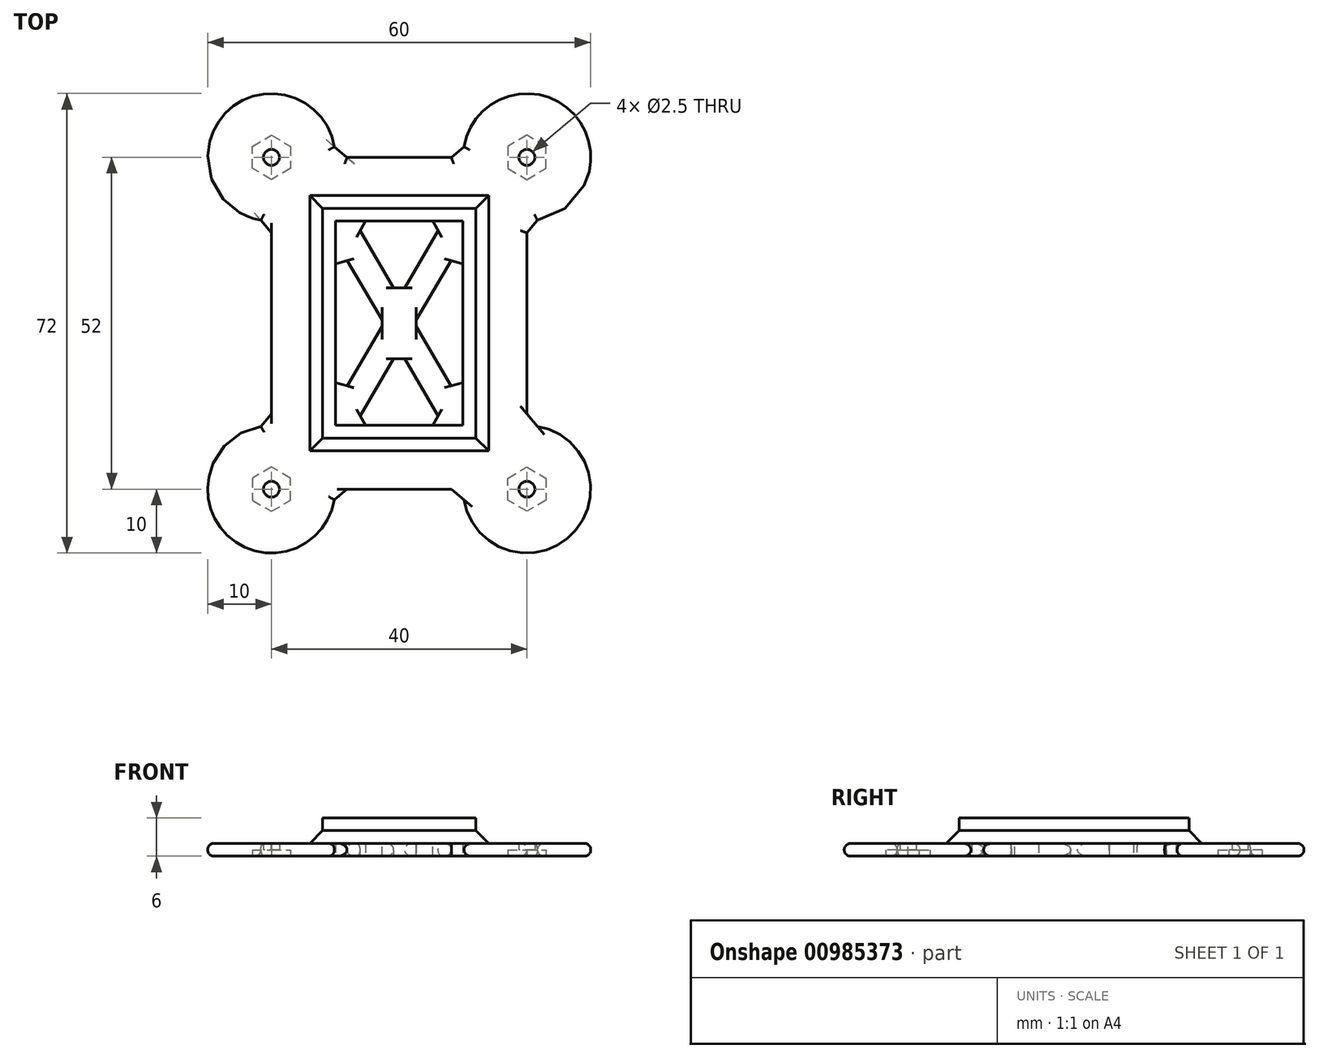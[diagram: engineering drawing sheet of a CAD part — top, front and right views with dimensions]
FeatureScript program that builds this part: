
annotation { "Feature Type Name" : "Feature", "Feature Type Description" : "" }
export const myFeature = defineFeature(function(context is Context, id is Id, definition is map)
    precondition{}
    {
        {
            var Q0;
            Q0=qCreatedBy(makeId("Top.planeOp"),FACE);
            var sketch = newSketch(context, id + "F0", { "sketchPlane" : qUnion([Q0])});
            skPoint(sketch, "E0.middle", {"position": v(0, 0) * mm});
            skLineSegment(sketch, "E1.bottom", {"start": v(10, -16) * mm, "end": v(-10, -16) * mm});
            skLineSegment(sketch, "E1.top", {"start": v(10, 16) * mm, "end": v(-10, 16) * mm});
            skLineSegment(sketch, "E1.left", {"start": v(10, -16) * mm, "end": v(10, 16) * mm});
            skLineSegment(sketch, "E1.right", {"start": v(-10, -16) * mm, "end": v(-10, 16) * mm});
            skLineSegment(sketch, "E2.bottom", {"start": v(12, 18) * mm, "end": v(-12, 18) * mm});
            skLineSegment(sketch, "E2.top", {"start": v(12, -18) * mm, "end": v(-12, -18) * mm});
            skLineSegment(sketch, "E2.left", {"start": v(12, 18) * mm, "end": v(12, -18) * mm});
            skLineSegment(sketch, "E2.right", {"start": v(-12, 18) * mm, "end": v(-12, -18) * mm});
            skLineSegment(sketch, "E3.bottom", {"start": v(20, -26) * mm, "end": v(-20, -26) * mm});
            skLineSegment(sketch, "E3.top", {"start": v(20, 26) * mm, "end": v(-20, 26) * mm});
            skLineSegment(sketch, "E3.left", {"start": v(20, -26) * mm, "end": v(20, 26) * mm});
            skLineSegment(sketch, "E3.right", {"start": v(-20, -26) * mm, "end": v(-20, 26) * mm});
            skCircle(sketch, "E4", {"center": v(-20, 26) * mm, "radius": 10 * mm});
            skCircle(sketch, "E5", {"center": v(20, 26) * mm, "radius": 10 * mm});
            skCircle(sketch, "E6", {"center": v(20, -26) * mm, "radius": 10 * mm});
            skCircle(sketch, "E7", {"center": v(-20, -26) * mm, "radius": 10 * mm});
            skCircle(sketch, "E8", {"center": v(-20, 26) * mm, "radius": 1.25 * mm});
            skCircle(sketch, "E9.MirrorC", {"center": v(20, 26) * mm, "radius": 1.25 * mm});
            skCircle(sketch, "E10.MirrorC", {"center": v(-20, -26) * mm, "radius": 1.25 * mm});
            skCircle(sketch, "E11.MirrorC", {"center": v(20, -26) * mm, "radius": 1.25 * mm});
            skCircle(sketch, "E12.cCircle", {"center": v(20, -26) * mm, "radius": 3 * mm, "construction": true});
            skLineSegment(sketch, "E12.0", {"start": v(23, -24.27) * mm, "end": v(23, -27.73) * mm});
            skLineSegment(sketch, "E12.1", {"start": v(23, -27.73) * mm, "end": v(20, -29.46) * mm});
            skLineSegment(sketch, "E12.2", {"start": v(20, -29.46) * mm, "end": v(17, -27.73) * mm});
            skLineSegment(sketch, "E12.3", {"start": v(17, -27.73) * mm, "end": v(17, -24.27) * mm});
            skLineSegment(sketch, "E12.4", {"start": v(17, -24.27) * mm, "end": v(20, -22.54) * mm});
            skLineSegment(sketch, "E12.5", {"start": v(20, -22.54) * mm, "end": v(23, -24.27) * mm});
            skPoint(sketch, "E12.0.midPoint", {"position": v(23, -26) * mm});
            skLineSegment(sketch, "E13.MirrorCS", {"start": v(-17, -27.73) * mm, "end": v(-17, -24.27) * mm});
            skLineSegment(sketch, "E14.MirrorCS", {"start": v(-20, -22.54) * mm, "end": v(-23, -24.27) * mm});
            skLineSegment(sketch, "E15.MirrorCS", {"start": v(-20, -29.46) * mm, "end": v(-17, -27.73) * mm});
            skLineSegment(sketch, "E16.MirrorCS", {"start": v(-23, -27.73) * mm, "end": v(-20, -29.46) * mm});
            skCircle(sketch, "E17.MirrorC", {"center": v(-20, -26) * mm, "radius": 3 * mm, "construction": true});
            skLineSegment(sketch, "E18.MirrorCS", {"start": v(-20, -26) * mm, "end": v(20, -26) * mm});
            skLineSegment(sketch, "E19.MirrorCS", {"start": v(-23, -24.27) * mm, "end": v(-23, -27.73) * mm});
            skLineSegment(sketch, "E20.MirrorCS", {"start": v(-17, -24.27) * mm, "end": v(-20, -22.54) * mm});
            skPoint(sketch, "E21.MirrorP", {"position": v(-23, -26) * mm});
            skCircle(sketch, "E22.MirrorC", {"center": v(20, 26) * mm, "radius": 3 * mm, "construction": true});
            skPoint(sketch, "E23.MirrorP", {"position": v(23, 26) * mm});
            skLineSegment(sketch, "E24.MirrorCS", {"start": v(20, 22.54) * mm, "end": v(23, 24.27) * mm});
            skLineSegment(sketch, "E25.MirrorCS", {"start": v(23, 27.73) * mm, "end": v(20, 29.46) * mm});
            skLineSegment(sketch, "E26.MirrorCS", {"start": v(23, 24.27) * mm, "end": v(23, 27.73) * mm});
            skLineSegment(sketch, "E27.MirrorCS", {"start": v(17, 27.73) * mm, "end": v(17, 24.27) * mm});
            skLineSegment(sketch, "E28.MirrorCS", {"start": v(17, 24.27) * mm, "end": v(20, 22.54) * mm});
            skLineSegment(sketch, "E29.MirrorCS", {"start": v(20, 29.46) * mm, "end": v(17, 27.73) * mm});
            skCircle(sketch, "E30.MirrorC", {"center": v(-20, 26) * mm, "radius": 3 * mm, "construction": true});
            skLineSegment(sketch, "E31.MirrorCS", {"start": v(-20, 26) * mm, "end": v(20, 26) * mm});
            skPoint(sketch, "E32.MirrorP", {"position": v(-23, 26) * mm});
            skLineSegment(sketch, "E33.MirrorCS", {"start": v(-20, 22.54) * mm, "end": v(-23, 24.27) * mm});
            skLineSegment(sketch, "E34.MirrorCS", {"start": v(-20, 26) * mm, "end": v(-20, -26) * mm});
            skLineSegment(sketch, "E35.MirrorCS", {"start": v(-23, 24.27) * mm, "end": v(-23, 27.73) * mm});
            skLineSegment(sketch, "E36.MirrorCS", {"start": v(-23, 27.73) * mm, "end": v(-20, 29.46) * mm});
            skLineSegment(sketch, "E37.MirrorCS", {"start": v(-17, 24.27) * mm, "end": v(-20, 22.54) * mm});
            skLineSegment(sketch, "E38.MirrorCS", {"start": v(-20, 29.46) * mm, "end": v(-17, 27.73) * mm});
            skLineSegment(sketch, "E39.MirrorCS", {"start": v(-17, 27.73) * mm, "end": v(-17, 24.27) * mm});
            skLineSegment(sketch, "E40", {"start": v(-10, 13) * mm, "end": v(7, -16) * mm});
            skLineSegment(sketch, "E41", {"start": v(-7, 16) * mm, "end": v(10, -13) * mm});
            skLineSegment(sketch, "E42", {"start": v(10, 13) * mm, "end": v(-7, -16) * mm});
            skLineSegment(sketch, "E43", {"start": v(7, 16) * mm, "end": v(-10, -13) * mm});
            skSolve(sketch);
        }
        {
            var Q0;
            Q0=makeQuery(id+"F0.imprint","IMPRINT",FACE,{"disambiguationData":[TD([[makeQuery(id+"F0.imprint","IMPRINT",EDGE,{"derivedFrom":sQuery(id+"F0.wireOp",EDGE,"E1.bottom")}),1.0]])]});
            var Q1;
            {var subQ0=sQuery(id+"F0.wireOp",EDGE,"XfmaCdGe-Nsh5-LR8N-U050-nXJdRo87k7nu");Q1=makeQuery(id+"F0.imprint","IMPRINT",FACE,{"disambiguationData":[TD([[makeQuery(id+"F0.imprint","IMPRINT",EDGE,{"derivedFrom":subQ0}),-1.0]])]});}
            var Q2;
            {var subQ0=sQuery(id+"F0.wireOp",EDGE,"67c493aa-9df7-43f4-b791-e47cdcb916b60.MirrorCS");Q2=makeQuery(id+"F0.imprint","IMPRINT",FACE,{"disambiguationData":[TD([[makeQuery(id+"F0.imprint","IMPRINT",EDGE,{"derivedFrom":subQ0}),-1.0]])]});}
            var Q3;
            {var subQ0=sQuery(id+"F0.wireOp",EDGE,"3c266ea2-0ddf-4ded-b89f-077357a7d8e80.MirrorCS");Q3=makeQuery(id+"F0.imprint","IMPRINT",FACE,{"disambiguationData":[TD([[makeQuery(id+"F0.imprint","IMPRINT",EDGE,{"derivedFrom":subQ0}),-1.0]])]});}
            var Q4;
            {var subQ0=sQuery(id+"F0.wireOp",EDGE,"ab4d64e5-a29a-4c87-9f54-f3676ced8fba0.MirrorCS");Q4=makeQuery(id+"F0.imprint","IMPRINT",FACE,{"disambiguationData":[TD([[makeQuery(id+"F0.imprint","IMPRINT",EDGE,{"derivedFrom":subQ0}),1.0]])]});}
            var Q5;
            Q5=makeQuery(id+"F0.imprint","IMPRINT",FACE,{"disambiguationData":[TD([[makeQuery(id+"F0.imprint","IMPRINT",EDGE,{"derivedFrom":sQuery(id+"F0.wireOp",EDGE,"oP3ZfhLO-5z78-oQSo-uuvH-yzJxo6IJEnQO")}),-1.0]])]});
            var Q6;
            Q6=makeQuery(id+"F0.imprint","IMPRINT",FACE,{"disambiguationData":[TD([[makeQuery(id+"F0.imprint","IMPRINT",EDGE,{"derivedFrom":sQuery(id+"F0.wireOp",EDGE,"5d5cfb4f-1e90-434a-910e-95713f9e32be0.MirrorC")}),1.0]])]});
            var Q7;
            Q7=makeQuery(id+"F0.imprint","IMPRINT",FACE,{"disambiguationData":[TD([[makeQuery(id+"F0.imprint","IMPRINT",EDGE,{"derivedFrom":sQuery(id+"F0.wireOp",EDGE,"24c43ebd-9ed0-4dd5-8c82-3635907a6bdc0.MirrorC")}),-1.0]])]});
            var Q8;
            Q8=makeQuery(id+"F0.imprint","IMPRINT",FACE,{"disambiguationData":[TD([[makeQuery(id+"F0.imprint","IMPRINT",EDGE,{"derivedFrom":sQuery(id+"F0.wireOp",EDGE,"ed7e95fd-fa47-4424-be7c-35b6ced3335c0.MirrorC")}),1.0]])]});
            var Q9;
            Q9=makeQuery(id+"F0.imprint","IMPRINT",FACE,{"disambiguationData":[TD([[makeQuery(id+"F0.imprint","IMPRINT",EDGE,{"derivedFrom":sQuery(id+"F0.wireOp",EDGE,"E2.bottom")}),-1.0]])]});
            var Q10;
            {var subQ0=sQuery(id+"F0.wireOp",EDGE,"E4");var subQ1=sQuery(id+"F0.wireOp",EDGE,"E3.top");var subQ2=makeQuery(id+"F0.imprint","INTERSECT",VERTEX,{"derivedFrom":[subQ1,subQ0]});Q10=makeQuery(id+"F0.imprint","IMPRINT",FACE,{"disambiguationData":[TD([[makeQuery(id+"F0.imprint","IMPRINT",EDGE,{"disambiguationData":[TD([[subQ2,-1.0]])],"derivedFrom":subQ1}),1.0]])]});}
            var Q11;
            {var subQ0=sQuery(id+"F0.wireOp",EDGE,"E4");var subQ1=sQuery(id+"F0.wireOp",EDGE,"E3.top");var subQ2=makeQuery(id+"F0.imprint","INTERSECT",VERTEX,{"derivedFrom":[subQ1,subQ0]});Q11=makeQuery(id+"F0.imprint","IMPRINT",FACE,{"disambiguationData":[TD([[makeQuery(id+"F0.imprint","IMPRINT",EDGE,{"disambiguationData":[TD([[subQ2,-1.0]])],"derivedFrom":subQ1}),-1.0]])]});}
            var Q12;
            {var subQ0=sQuery(id+"F0.wireOp",EDGE,"E5");var subQ1=sQuery(id+"F0.wireOp",EDGE,"E3.top");var subQ2=makeQuery(id+"F0.imprint","INTERSECT",VERTEX,{"derivedFrom":[subQ1,subQ0]});Q12=makeQuery(id+"F0.imprint","IMPRINT",FACE,{"disambiguationData":[TD([[makeQuery(id+"F0.imprint","IMPRINT",EDGE,{"disambiguationData":[TD([[subQ2,1.0]])],"derivedFrom":subQ1}),1.0]])]});}
            var Q13;
            {var subQ0=sQuery(id+"F0.wireOp",EDGE,"E5");var subQ1=sQuery(id+"F0.wireOp",EDGE,"E3.top");var subQ2=makeQuery(id+"F0.imprint","INTERSECT",VERTEX,{"derivedFrom":[subQ1,subQ0]});Q13=makeQuery(id+"F0.imprint","IMPRINT",FACE,{"disambiguationData":[TD([[makeQuery(id+"F0.imprint","IMPRINT",EDGE,{"disambiguationData":[TD([[subQ2,1.0]])],"derivedFrom":subQ1}),-1.0]])]});}
            var Q14;
            {var subQ0=sQuery(id+"F0.wireOp",EDGE,"E6");var subQ1=sQuery(id+"F0.wireOp",EDGE,"E3.bottom");var subQ2=makeQuery(id+"F0.imprint","INTERSECT",VERTEX,{"derivedFrom":[subQ1,subQ0]});Q14=makeQuery(id+"F0.imprint","IMPRINT",FACE,{"disambiguationData":[TD([[makeQuery(id+"F0.imprint","IMPRINT",EDGE,{"disambiguationData":[TD([[subQ2,1.0]])],"derivedFrom":subQ1}),-1.0]])]});}
            var Q15;
            {var subQ0=sQuery(id+"F0.wireOp",EDGE,"E6");var subQ1=sQuery(id+"F0.wireOp",EDGE,"E3.bottom");var subQ2=makeQuery(id+"F0.imprint","INTERSECT",VERTEX,{"derivedFrom":[subQ1,subQ0]});Q15=makeQuery(id+"F0.imprint","IMPRINT",FACE,{"disambiguationData":[TD([[makeQuery(id+"F0.imprint","IMPRINT",EDGE,{"disambiguationData":[TD([[subQ2,1.0]])],"derivedFrom":subQ1}),1.0]])]});}
            var Q16;
            {var subQ0=sQuery(id+"F0.wireOp",EDGE,"E7");var subQ1=sQuery(id+"F0.wireOp",EDGE,"E3.bottom");var subQ2=makeQuery(id+"F0.imprint","INTERSECT",VERTEX,{"derivedFrom":[subQ1,subQ0]});Q16=makeQuery(id+"F0.imprint","IMPRINT",FACE,{"disambiguationData":[TD([[makeQuery(id+"F0.imprint","IMPRINT",EDGE,{"disambiguationData":[TD([[subQ2,-1.0]])],"derivedFrom":subQ1}),1.0]])]});}
            var Q17;
            {var subQ0=sQuery(id+"F0.wireOp",EDGE,"E7");var subQ1=sQuery(id+"F0.wireOp",EDGE,"E3.bottom");var subQ2=makeQuery(id+"F0.imprint","INTERSECT",VERTEX,{"derivedFrom":[subQ1,subQ0]});Q17=makeQuery(id+"F0.imprint","IMPRINT",FACE,{"disambiguationData":[TD([[makeQuery(id+"F0.imprint","IMPRINT",EDGE,{"disambiguationData":[TD([[subQ2,-1.0]])],"derivedFrom":subQ1}),-1.0]])]});}
            var Q18;
            {var subQ0=sQuery(id+"F0.wireOp",EDGE,"E15.MirrorCS");Q18=makeQuery(id+"F0.imprint","IMPRINT",FACE,{"disambiguationData":[TD([[makeQuery(id+"F0.imprint","IMPRINT",EDGE,{"derivedFrom":subQ0}),-1.0]])]});}
            var Q19;
            {var subQ0=sQuery(id+"F0.wireOp",EDGE,"E12.4");Q19=makeQuery(id+"F0.imprint","IMPRINT",FACE,{"disambiguationData":[TD([[makeQuery(id+"F0.imprint","IMPRINT",EDGE,{"derivedFrom":subQ0}),1.0]])]});}
            var Q20;
            Q20=makeQuery(id+"F0.imprint","IMPRINT",FACE,{"disambiguationData":[TD([[makeQuery(id+"F0.imprint","IMPRINT",EDGE,{"derivedFrom":sQuery(id+"F0.wireOp",EDGE,"E12.0")}),1.0]])]});
            var Q21;
            {var subQ5=sQuery(id+"F0.wireOp",EDGE,"E20.MirrorCS");Q21=makeQuery(id+"F0.imprint","IMPRINT",FACE,{"disambiguationData":[TD([[makeQuery(id+"F0.imprint","IMPRINT",EDGE,{"derivedFrom":subQ5}),-1.0]])]});}
            var Q22;
            {var subQ0=sQuery(id+"F0.wireOp",EDGE,"E38.MirrorCS");Q22=makeQuery(id+"F0.imprint","IMPRINT",FACE,{"disambiguationData":[TD([[makeQuery(id+"F0.imprint","IMPRINT",EDGE,{"derivedFrom":subQ0}),1.0]])]});}
            var Q23;
            {var subQ0=sQuery(id+"F0.wireOp",EDGE,"E37.MirrorCS");Q23=makeQuery(id+"F0.imprint","IMPRINT",FACE,{"disambiguationData":[TD([[makeQuery(id+"F0.imprint","IMPRINT",EDGE,{"derivedFrom":subQ0}),1.0]])]});}
            var Q24;
            {var subQ0=sQuery(id+"F0.wireOp",EDGE,"E28.MirrorCS");Q24=makeQuery(id+"F0.imprint","IMPRINT",FACE,{"disambiguationData":[TD([[makeQuery(id+"F0.imprint","IMPRINT",EDGE,{"derivedFrom":subQ0}),-1.0]])]});}
            var Q25;
            {var subQ5=sQuery(id+"F0.wireOp",EDGE,"E24.MirrorCS");Q25=makeQuery(id+"F0.imprint","IMPRINT",FACE,{"disambiguationData":[TD([[makeQuery(id+"F0.imprint","IMPRINT",EDGE,{"derivedFrom":subQ5}),-1.0]])]});}
            var Q26;
            {var subQ1=sQuery(id+"F0.wireOp",EDGE,"E1.left");var subQ5=sQuery(id+"F0.wireOp",EDGE,"E1.bottom");var subQ6=makeQuery(id+"F0.imprint","INTERSECT",VERTEX,{"derivedFrom":[subQ5,subQ1]});Q26=makeQuery(id+"F0.imprint","IMPRINT",FACE,{"disambiguationData":[TD([[makeQuery(id+"F0.imprint","IMPRINT",EDGE,{"disambiguationData":[TD([[subQ6,-1.0]])],"derivedFrom":subQ5}),-1.0]])]});}
            var Q27;
            {var subQ0=sQuery(id+"F0.wireOp",EDGE,"E43");var subQ1=sQuery(id+"F0.wireOp",EDGE,"E40");var subQ2=makeQuery(id+"F0.imprint","INTERSECT",VERTEX,{"derivedFrom":[subQ1,subQ0]});Q27=makeQuery(id+"F0.imprint","IMPRINT",FACE,{"disambiguationData":[TD([[makeQuery(id+"F0.imprint","IMPRINT",EDGE,{"disambiguationData":[TD([[subQ2,-1.0]])],"derivedFrom":subQ1}),1.0]])]});}
            var Q28;
            {var subQ1=sQuery(id+"F0.wireOp",EDGE,"E1.bottom");var subQ7=sQuery(id+"F0.wireOp",EDGE,"E1.right");var subQ8=makeQuery(id+"F0.imprint","INTERSECT",VERTEX,{"derivedFrom":[subQ1,subQ7]});Q28=makeQuery(id+"F0.imprint","IMPRINT",FACE,{"disambiguationData":[TD([[makeQuery(id+"F0.imprint","IMPRINT",EDGE,{"disambiguationData":[TD([[subQ8,1.0]])],"derivedFrom":subQ1}),-1.0]])]});}
            var Q29;
            {var subQ1=sQuery(id+"F0.wireOp",EDGE,"E1.left");var subQ7=sQuery(id+"F0.wireOp",EDGE,"E1.top");var subQ8=makeQuery(id+"F0.imprint","INTERSECT",VERTEX,{"derivedFrom":[subQ7,subQ1]});Q29=makeQuery(id+"F0.imprint","IMPRINT",FACE,{"disambiguationData":[TD([[makeQuery(id+"F0.imprint","IMPRINT",EDGE,{"disambiguationData":[TD([[subQ8,-1.0]])],"derivedFrom":subQ7}),1.0]])]});}
            var Q30;
            {var subQ1=sQuery(id+"F0.wireOp",EDGE,"E1.right");var subQ5=sQuery(id+"F0.wireOp",EDGE,"E1.top");var subQ6=makeQuery(id+"F0.imprint","INTERSECT",VERTEX,{"derivedFrom":[subQ5,subQ1]});Q30=makeQuery(id+"F0.imprint","IMPRINT",FACE,{"disambiguationData":[TD([[makeQuery(id+"F0.imprint","IMPRINT",EDGE,{"disambiguationData":[TD([[subQ6,1.0]])],"derivedFrom":subQ5}),1.0]])]});}
            extrude(context, id + "F1", {"entities" : qUnion([Q0, Q1, Q2, Q3, Q4, Q5, Q6, Q7, Q8, Q9, Q10, Q11, Q12, Q13, Q14, Q15, Q16, Q17, Q18, Q19, Q20, Q21, Q22, Q23, Q24, Q25, Q26, Q27, Q28, Q29, Q30]), "depth" : 2 * mm, "offsetDistance" : 25 * mm});
        }
        {
            var Q0;
            Q0=makeQuery(id+"F0.imprint","IMPRINT",FACE,{"disambiguationData":[TD([[makeQuery(id+"F0.imprint","IMPRINT",EDGE,{"derivedFrom":sQuery(id+"F0.wireOp",EDGE,"E1.bottom")}),1.0]])]});
            extrude(context, id + "F2", {"entities" : qUnion([Q0]), "operationType" : NewBodyOperationType.ADD, "depth" : 6 * mm, "offsetDistance" : 25 * mm});
        }
        {
            var Q0;
            Q0=makeQuery(id+"F2.boolean.opBoolean","INTERSECT",EDGE,{"derivedFrom":[makeQuery(id+"F1.opExtrude","CAP_FACE",FACE,{"disambiguationData":[OSD([sQuery(id+"F0.wireOp",EDGE,"E3.bottom"),sQuery(id+"F0.wireOp",EDGE,"E3.top"),sQuery(id+"F0.wireOp",EDGE,"E3.left"),sQuery(id+"F0.wireOp",EDGE,"E3.right"),sQuery(id+"F0.wireOp",EDGE,"E4"),sQuery(id+"F0.wireOp",EDGE,"E5"),sQuery(id+"F0.wireOp",EDGE,"E6"),sQuery(id+"F0.wireOp",EDGE,"E7"),sQuery(id+"F0.wireOp",EDGE,"E8"),sQuery(id+"F0.wireOp",EDGE,"E9.MirrorC"),sQuery(id+"F0.wireOp",EDGE,"E10.MirrorC"),sQuery(id+"F0.wireOp",EDGE,"E11.MirrorC")])],"isStart":false}),makeQuery(id+"F2.opExtrude","SWEPT_FACE",FACE,{"disambiguationData":[OSD([sQuery(id+"F0.wireOp",EDGE,"E2.right")])]})]});
            var Q1;
            Q1=makeQuery(id+"F2.boolean.opBoolean","INTERSECT",EDGE,{"derivedFrom":[makeQuery(id+"F1.opExtrude","CAP_FACE",FACE,{"disambiguationData":[OSD([sQuery(id+"F0.wireOp",EDGE,"E3.bottom"),sQuery(id+"F0.wireOp",EDGE,"E3.top"),sQuery(id+"F0.wireOp",EDGE,"E3.left"),sQuery(id+"F0.wireOp",EDGE,"E3.right"),sQuery(id+"F0.wireOp",EDGE,"E4"),sQuery(id+"F0.wireOp",EDGE,"E5"),sQuery(id+"F0.wireOp",EDGE,"E6"),sQuery(id+"F0.wireOp",EDGE,"E7"),sQuery(id+"F0.wireOp",EDGE,"E8"),sQuery(id+"F0.wireOp",EDGE,"E9.MirrorC"),sQuery(id+"F0.wireOp",EDGE,"E10.MirrorC"),sQuery(id+"F0.wireOp",EDGE,"E11.MirrorC")])],"isStart":false}),makeQuery(id+"F2.opExtrude","SWEPT_FACE",FACE,{"disambiguationData":[OSD([sQuery(id+"F0.wireOp",EDGE,"E2.top")])]})]});
            var Q2;
            Q2=makeQuery(id+"F2.boolean.opBoolean","INTERSECT",EDGE,{"derivedFrom":[makeQuery(id+"F1.opExtrude","CAP_FACE",FACE,{"disambiguationData":[OSD([sQuery(id+"F0.wireOp",EDGE,"E3.bottom"),sQuery(id+"F0.wireOp",EDGE,"E3.top"),sQuery(id+"F0.wireOp",EDGE,"E3.left"),sQuery(id+"F0.wireOp",EDGE,"E3.right"),sQuery(id+"F0.wireOp",EDGE,"E4"),sQuery(id+"F0.wireOp",EDGE,"E5"),sQuery(id+"F0.wireOp",EDGE,"E6"),sQuery(id+"F0.wireOp",EDGE,"E7"),sQuery(id+"F0.wireOp",EDGE,"E8"),sQuery(id+"F0.wireOp",EDGE,"E9.MirrorC"),sQuery(id+"F0.wireOp",EDGE,"E10.MirrorC"),sQuery(id+"F0.wireOp",EDGE,"E11.MirrorC")])],"isStart":false}),makeQuery(id+"F2.opExtrude","SWEPT_FACE",FACE,{"disambiguationData":[OSD([sQuery(id+"F0.wireOp",EDGE,"E2.left")])]})]});
            var Q3;
            Q3=makeQuery(id+"F2.boolean.opBoolean","INTERSECT",EDGE,{"derivedFrom":[makeQuery(id+"F1.opExtrude","CAP_FACE",FACE,{"disambiguationData":[OSD([sQuery(id+"F0.wireOp",EDGE,"E3.bottom"),sQuery(id+"F0.wireOp",EDGE,"E3.top"),sQuery(id+"F0.wireOp",EDGE,"E3.left"),sQuery(id+"F0.wireOp",EDGE,"E3.right"),sQuery(id+"F0.wireOp",EDGE,"E4"),sQuery(id+"F0.wireOp",EDGE,"E5"),sQuery(id+"F0.wireOp",EDGE,"E6"),sQuery(id+"F0.wireOp",EDGE,"E7"),sQuery(id+"F0.wireOp",EDGE,"E8"),sQuery(id+"F0.wireOp",EDGE,"E9.MirrorC"),sQuery(id+"F0.wireOp",EDGE,"E10.MirrorC"),sQuery(id+"F0.wireOp",EDGE,"E11.MirrorC")])],"isStart":false}),makeQuery(id+"F2.opExtrude","SWEPT_FACE",FACE,{"disambiguationData":[OSD([sQuery(id+"F0.wireOp",EDGE,"E2.bottom")])]})]});
            var Q4;
            Q4=makeQuery(id+"F1.opExtrude","SWEPT_EDGE",EDGE,{"disambiguationData":[OSD([sQuery(id+"F0.wireOp",EDGE,"E3.top"),sQuery(id+"F0.wireOp",EDGE,"E4")])]});
            var Q5;
            Q5=makeQuery(id+"F1.opExtrude","SWEPT_EDGE",EDGE,{"disambiguationData":[OSD([sQuery(id+"F0.wireOp",EDGE,"E3.top"),sQuery(id+"F0.wireOp",EDGE,"E5")])]});
            var Q6;
            Q6=makeQuery(id+"F1.opExtrude","SWEPT_EDGE",EDGE,{"disambiguationData":[OSD([sQuery(id+"F0.wireOp",EDGE,"E3.left"),sQuery(id+"F0.wireOp",EDGE,"E5")])]});
            var Q7;
            Q7=makeQuery(id+"F1.opExtrude","SWEPT_EDGE",EDGE,{"disambiguationData":[OSD([sQuery(id+"F0.wireOp",EDGE,"E3.left"),sQuery(id+"F0.wireOp",EDGE,"E6")])]});
            var Q8;
            Q8=makeQuery(id+"F1.opExtrude","SWEPT_EDGE",EDGE,{"disambiguationData":[OSD([sQuery(id+"F0.wireOp",EDGE,"E3.bottom"),sQuery(id+"F0.wireOp",EDGE,"E6")])]});
            var Q9;
            Q9=makeQuery(id+"F1.opExtrude","SWEPT_EDGE",EDGE,{"disambiguationData":[OSD([sQuery(id+"F0.wireOp",EDGE,"E3.bottom"),sQuery(id+"F0.wireOp",EDGE,"E7")])]});
            var Q10;
            Q10=makeQuery(id+"F1.opExtrude","SWEPT_EDGE",EDGE,{"disambiguationData":[OSD([sQuery(id+"F0.wireOp",EDGE,"E3.right"),sQuery(id+"F0.wireOp",EDGE,"E7")])]});
            var Q11;
            Q11=makeQuery(id+"F1.opExtrude","SWEPT_EDGE",EDGE,{"disambiguationData":[OSD([sQuery(id+"F0.wireOp",EDGE,"E3.right"),sQuery(id+"F0.wireOp",EDGE,"E4")])]});
            chamfer(context, id + "F3", {"entities" : qUnion([Q0, Q1, Q2, Q3, Q4, Q5, Q6, Q7, Q8, Q9, Q10, Q11]), "width" : 2 * mm, "tangentPropagation" : true});
        }
        {
            var Q0;
            Q0=makeQuery(id+"F1.opExtrude","CAP_EDGE",EDGE,{"disambiguationData":[OSD([sQuery(id+"F0.wireOp",EDGE,"E5")])],"isStart":false});
            var Q1;
            Q1=makeQuery(id+"F1.opExtrude","CAP_EDGE",EDGE,{"disambiguationData":[OSD([sQuery(id+"F0.wireOp",EDGE,"E5")])],"isStart":true});
            var Q2;
            {var subQ0=sQuery(id+"F0.wireOp",EDGE,"E26.MirrorCS");var subQ1=sQuery(id+"F0.wireOp",EDGE,"E25.MirrorCS");var subQ2=sQuery(id+"F0.wireOp",EDGE,"E24.MirrorCS");var subQ3=sQuery(id+"F0.wireOp",EDGE,"E19.MirrorCS");var subQ4=sQuery(id+"F0.wireOp",EDGE,"E16.MirrorCS");var subQ5=sQuery(id+"F0.wireOp",EDGE,"E14.MirrorCS");var subQ6=sQuery(id+"F0.wireOp",EDGE,"E20.MirrorCS");var subQ7=sQuery(id+"F0.wireOp",EDGE,"E18.MirrorCS");var subQ8=sQuery(id+"F0.wireOp",EDGE,"E15.MirrorCS");var subQ9=sQuery(id+"F0.wireOp",EDGE,"E13.MirrorCS");var subQ10=sQuery(id+"F0.wireOp",EDGE,"E12.5");var subQ11=sQuery(id+"F0.wireOp",EDGE,"E5");var subQ12=sQuery(id+"F0.wireOp",EDGE,"E4");var subQ13=sQuery(id+"F0.wireOp",EDGE,"E6");var subQ14=sQuery(id+"F0.wireOp",EDGE,"E27.MirrorCS");var subQ15=sQuery(id+"F0.wireOp",EDGE,"E3.left");var subQ16=sQuery(id+"F0.wireOp",EDGE,"E12.4");var subQ17=sQuery(id+"F0.wireOp",EDGE,"E7");var subQ18=sQuery(id+"F0.wireOp",EDGE,"E12.0");var subQ19=sQuery(id+"F0.wireOp",EDGE,"E12.1");var subQ20=sQuery(id+"F0.wireOp",EDGE,"E12.2");var subQ21=sQuery(id+"F0.wireOp",EDGE,"E12.3");var subQ22=sQuery(id+"F0.wireOp",EDGE,"E28.MirrorCS");var subQ23=sQuery(id+"F0.wireOp",EDGE,"E29.MirrorCS");var subQ24=sQuery(id+"F0.wireOp",EDGE,"E3.top");var subQ25=sQuery(id+"F0.wireOp",EDGE,"E34.MirrorCS");var subQ26=sQuery(id+"F0.wireOp",EDGE,"E37.MirrorCS");var subQ27=sQuery(id+"F0.wireOp",EDGE,"E38.MirrorCS");var subQ28=sQuery(id+"F0.wireOp",EDGE,"E35.MirrorCS");var subQ29=sQuery(id+"F0.wireOp",EDGE,"E36.MirrorCS");var subQ30=sQuery(id+"F0.wireOp",EDGE,"E33.MirrorCS");var subQ31=sQuery(id+"F0.wireOp",EDGE,"E39.MirrorCS");Q2=makeQuery(id+"F3.opChamfer","BLEND_EDGE",EDGE,{"blendedFrom":[makeQuery(id+"F1.opExtrude","SWEPT_EDGE",EDGE,{"disambiguationData":[OSD([subQ15,subQ11])]}),makeQuery(id+"F2.boolean.opBoolean","SPLIT",FACE,{"disambiguationData":[TD([makeQuery(id+"F1.opExtrude","SWEPT_FACE",FACE,{"disambiguationData":[OSD([subQ15])]})])],"derivedFrom":makeQuery(id+"F1.opExtrude","CAP_FACE",FACE,{"disambiguationData":[OSD([subQ15,subQ12,subQ11,subQ13,subQ17,subQ18,subQ19,subQ20,subQ21,subQ16,subQ10,subQ9,subQ8,subQ7,subQ6,subQ5,subQ4,subQ3,subQ2,subQ1,subQ0,subQ14,subQ22,subQ23,subQ24,subQ25,subQ26,subQ27,subQ28,subQ29,subQ30,subQ31])],"isStart":false})})],"blendedInto":[makeQuery(id+"F2.boolean.opBoolean","SPLIT",FACE,{"disambiguationData":[TD([makeQuery(id+"F1.opExtrude","SWEPT_FACE",FACE,{"disambiguationData":[OSD([subQ15])]})])],"derivedFrom":makeQuery(id+"F1.opExtrude","CAP_FACE",FACE,{"disambiguationData":[OSD([subQ15,subQ12,subQ11,subQ13,subQ17,subQ18,subQ19,subQ20,subQ21,subQ16,subQ10,subQ9,subQ8,subQ7,subQ6,subQ5,subQ4,subQ3,subQ2,subQ1,subQ0,subQ14,subQ22,subQ23,subQ24,subQ25,subQ26,subQ27,subQ28,subQ29,subQ30,subQ31])],"isStart":false})})]});}
            var Q3;
            {var subQ0=sQuery(id+"F0.wireOp",EDGE,"E5");var subQ1=sQuery(id+"F0.wireOp",EDGE,"E3.left");Q3=makeQuery(id+"F3.opChamfer","BLEND_EDGE",EDGE,{"blendedFrom":[makeQuery(id+"F1.opExtrude","SWEPT_EDGE",EDGE,{"disambiguationData":[OSD([subQ1,subQ0])]}),makeQuery(id+"F1.opExtrude","CAP_FACE",FACE,{"disambiguationData":[OSD([subQ1,sQuery(id+"F0.wireOp",EDGE,"E4"),subQ0,sQuery(id+"F0.wireOp",EDGE,"E6"),sQuery(id+"F0.wireOp",EDGE,"E7"),sQuery(id+"F0.wireOp",EDGE,"E12.0"),sQuery(id+"F0.wireOp",EDGE,"E12.1"),sQuery(id+"F0.wireOp",EDGE,"E12.2"),sQuery(id+"F0.wireOp",EDGE,"E12.3"),sQuery(id+"F0.wireOp",EDGE,"E12.4"),sQuery(id+"F0.wireOp",EDGE,"E12.5"),sQuery(id+"F0.wireOp",EDGE,"E13.MirrorCS"),sQuery(id+"F0.wireOp",EDGE,"E15.MirrorCS"),sQuery(id+"F0.wireOp",EDGE,"E18.MirrorCS"),sQuery(id+"F0.wireOp",EDGE,"E20.MirrorCS"),sQuery(id+"F0.wireOp",EDGE,"E14.MirrorCS"),sQuery(id+"F0.wireOp",EDGE,"E16.MirrorCS"),sQuery(id+"F0.wireOp",EDGE,"E19.MirrorCS"),sQuery(id+"F0.wireOp",EDGE,"E24.MirrorCS"),sQuery(id+"F0.wireOp",EDGE,"E25.MirrorCS"),sQuery(id+"F0.wireOp",EDGE,"E26.MirrorCS"),sQuery(id+"F0.wireOp",EDGE,"E27.MirrorCS"),sQuery(id+"F0.wireOp",EDGE,"E28.MirrorCS"),sQuery(id+"F0.wireOp",EDGE,"E29.MirrorCS"),sQuery(id+"F0.wireOp",EDGE,"E3.top"),sQuery(id+"F0.wireOp",EDGE,"E34.MirrorCS"),sQuery(id+"F0.wireOp",EDGE,"E37.MirrorCS"),sQuery(id+"F0.wireOp",EDGE,"E38.MirrorCS"),sQuery(id+"F0.wireOp",EDGE,"E35.MirrorCS"),sQuery(id+"F0.wireOp",EDGE,"E36.MirrorCS"),sQuery(id+"F0.wireOp",EDGE,"E33.MirrorCS"),sQuery(id+"F0.wireOp",EDGE,"E39.MirrorCS")])],"isStart":true})],"blendedInto":[makeQuery(id+"F1.opExtrude","CAP_FACE",FACE,{"disambiguationData":[OSD([subQ1,sQuery(id+"F0.wireOp",EDGE,"E4"),subQ0,sQuery(id+"F0.wireOp",EDGE,"E6"),sQuery(id+"F0.wireOp",EDGE,"E7"),sQuery(id+"F0.wireOp",EDGE,"E12.0"),sQuery(id+"F0.wireOp",EDGE,"E12.1"),sQuery(id+"F0.wireOp",EDGE,"E12.2"),sQuery(id+"F0.wireOp",EDGE,"E12.3"),sQuery(id+"F0.wireOp",EDGE,"E12.4"),sQuery(id+"F0.wireOp",EDGE,"E12.5"),sQuery(id+"F0.wireOp",EDGE,"E13.MirrorCS"),sQuery(id+"F0.wireOp",EDGE,"E15.MirrorCS"),sQuery(id+"F0.wireOp",EDGE,"E18.MirrorCS"),sQuery(id+"F0.wireOp",EDGE,"E20.MirrorCS"),sQuery(id+"F0.wireOp",EDGE,"E14.MirrorCS"),sQuery(id+"F0.wireOp",EDGE,"E16.MirrorCS"),sQuery(id+"F0.wireOp",EDGE,"E19.MirrorCS"),sQuery(id+"F0.wireOp",EDGE,"E24.MirrorCS"),sQuery(id+"F0.wireOp",EDGE,"E25.MirrorCS"),sQuery(id+"F0.wireOp",EDGE,"E26.MirrorCS"),sQuery(id+"F0.wireOp",EDGE,"E27.MirrorCS"),sQuery(id+"F0.wireOp",EDGE,"E28.MirrorCS"),sQuery(id+"F0.wireOp",EDGE,"E29.MirrorCS"),sQuery(id+"F0.wireOp",EDGE,"E3.top"),sQuery(id+"F0.wireOp",EDGE,"E34.MirrorCS"),sQuery(id+"F0.wireOp",EDGE,"E37.MirrorCS"),sQuery(id+"F0.wireOp",EDGE,"E38.MirrorCS"),sQuery(id+"F0.wireOp",EDGE,"E35.MirrorCS"),sQuery(id+"F0.wireOp",EDGE,"E36.MirrorCS"),sQuery(id+"F0.wireOp",EDGE,"E33.MirrorCS"),sQuery(id+"F0.wireOp",EDGE,"E39.MirrorCS")])],"isStart":true})]});}
            var Q4;
            Q4=makeQuery(id+"F1.opExtrude","CAP_EDGE",EDGE,{"disambiguationData":[OSD([sQuery(id+"F0.wireOp",EDGE,"E3.left")])],"isStart":false});
            var Q5;
            Q5=makeQuery(id+"F1.opExtrude","CAP_EDGE",EDGE,{"disambiguationData":[OSD([sQuery(id+"F0.wireOp",EDGE,"E3.left")])],"isStart":true});
            var Q6;
            Q6=makeQuery(id+"F1.opExtrude","CAP_EDGE",EDGE,{"disambiguationData":[OSD([sQuery(id+"F0.wireOp",EDGE,"E6")])],"isStart":false});
            var Q7;
            Q7=makeQuery(id+"F1.opExtrude","CAP_EDGE",EDGE,{"disambiguationData":[OSD([sQuery(id+"F0.wireOp",EDGE,"E6")])],"isStart":true});
            var Q8;
            Q8=makeQuery(id+"F1.opExtrude","SWEPT_FACE",FACE,{"disambiguationData":[OSD([sQuery(id+"F0.wireOp",EDGE,"E18.MirrorCS")])]});
            var Q9;
            Q9=makeQuery(id+"F1.opExtrude","CAP_EDGE",EDGE,{"disambiguationData":[OSD([sQuery(id+"F0.wireOp",EDGE,"E7")])],"isStart":false});
            var Q10;
            Q10=makeQuery(id+"F1.opExtrude","CAP_EDGE",EDGE,{"disambiguationData":[OSD([sQuery(id+"F0.wireOp",EDGE,"E7")])],"isStart":true});
            var Q11;
            Q11=makeQuery(id+"F1.opExtrude","CAP_EDGE",EDGE,{"disambiguationData":[OSD([sQuery(id+"F0.wireOp",EDGE,"E34.MirrorCS")])],"isStart":false});
            var Q12;
            Q12=makeQuery(id+"F1.opExtrude","CAP_EDGE",EDGE,{"disambiguationData":[OSD([sQuery(id+"F0.wireOp",EDGE,"E34.MirrorCS")])],"isStart":true});
            var Q13;
            {var subQ0=sQuery(id+"F0.wireOp",EDGE,"E26.MirrorCS");var subQ1=sQuery(id+"F0.wireOp",EDGE,"E25.MirrorCS");var subQ2=sQuery(id+"F0.wireOp",EDGE,"E24.MirrorCS");var subQ3=sQuery(id+"F0.wireOp",EDGE,"E19.MirrorCS");var subQ4=sQuery(id+"F0.wireOp",EDGE,"E16.MirrorCS");var subQ5=sQuery(id+"F0.wireOp",EDGE,"E14.MirrorCS");var subQ6=sQuery(id+"F0.wireOp",EDGE,"E20.MirrorCS");var subQ7=sQuery(id+"F0.wireOp",EDGE,"E18.MirrorCS");var subQ8=sQuery(id+"F0.wireOp",EDGE,"E15.MirrorCS");var subQ9=sQuery(id+"F0.wireOp",EDGE,"E13.MirrorCS");var subQ10=sQuery(id+"F0.wireOp",EDGE,"E12.5");var subQ11=sQuery(id+"F0.wireOp",EDGE,"E5");var subQ12=sQuery(id+"F0.wireOp",EDGE,"E4");var subQ13=sQuery(id+"F0.wireOp",EDGE,"E6");var subQ14=sQuery(id+"F0.wireOp",EDGE,"E27.MirrorCS");var subQ15=sQuery(id+"F0.wireOp",EDGE,"E3.left");var subQ16=sQuery(id+"F0.wireOp",EDGE,"E12.4");var subQ17=sQuery(id+"F0.wireOp",EDGE,"E7");var subQ18=sQuery(id+"F0.wireOp",EDGE,"E12.0");var subQ19=sQuery(id+"F0.wireOp",EDGE,"E12.1");var subQ20=sQuery(id+"F0.wireOp",EDGE,"E12.2");var subQ21=sQuery(id+"F0.wireOp",EDGE,"E12.3");var subQ22=sQuery(id+"F0.wireOp",EDGE,"E28.MirrorCS");var subQ23=sQuery(id+"F0.wireOp",EDGE,"E29.MirrorCS");var subQ24=sQuery(id+"F0.wireOp",EDGE,"E3.top");var subQ25=sQuery(id+"F0.wireOp",EDGE,"E34.MirrorCS");var subQ26=sQuery(id+"F0.wireOp",EDGE,"E37.MirrorCS");var subQ27=sQuery(id+"F0.wireOp",EDGE,"E38.MirrorCS");var subQ28=sQuery(id+"F0.wireOp",EDGE,"E35.MirrorCS");var subQ29=sQuery(id+"F0.wireOp",EDGE,"E36.MirrorCS");var subQ30=sQuery(id+"F0.wireOp",EDGE,"E33.MirrorCS");var subQ31=sQuery(id+"F0.wireOp",EDGE,"E39.MirrorCS");Q13=makeQuery(id+"F3.opChamfer","BLEND_EDGE",EDGE,{"blendedFrom":[makeQuery(id+"F1.opExtrude","SWEPT_EDGE",EDGE,{"disambiguationData":[OSD([subQ17,subQ25])]}),makeQuery(id+"F2.boolean.opBoolean","SPLIT",FACE,{"disambiguationData":[TD([makeQuery(id+"F1.opExtrude","SWEPT_FACE",FACE,{"disambiguationData":[OSD([subQ15])]})])],"derivedFrom":makeQuery(id+"F1.opExtrude","CAP_FACE",FACE,{"disambiguationData":[OSD([subQ15,subQ12,subQ11,subQ13,subQ17,subQ18,subQ19,subQ20,subQ21,subQ16,subQ10,subQ9,subQ8,subQ7,subQ6,subQ5,subQ4,subQ3,subQ2,subQ1,subQ0,subQ14,subQ22,subQ23,subQ24,subQ25,subQ26,subQ27,subQ28,subQ29,subQ30,subQ31])],"isStart":false})})],"blendedInto":[makeQuery(id+"F2.boolean.opBoolean","SPLIT",FACE,{"disambiguationData":[TD([makeQuery(id+"F1.opExtrude","SWEPT_FACE",FACE,{"disambiguationData":[OSD([subQ15])]})])],"derivedFrom":makeQuery(id+"F1.opExtrude","CAP_FACE",FACE,{"disambiguationData":[OSD([subQ15,subQ12,subQ11,subQ13,subQ17,subQ18,subQ19,subQ20,subQ21,subQ16,subQ10,subQ9,subQ8,subQ7,subQ6,subQ5,subQ4,subQ3,subQ2,subQ1,subQ0,subQ14,subQ22,subQ23,subQ24,subQ25,subQ26,subQ27,subQ28,subQ29,subQ30,subQ31])],"isStart":false})})]});}
            var Q14;
            {var subQ0=sQuery(id+"F0.wireOp",EDGE,"E34.MirrorCS");var subQ1=sQuery(id+"F0.wireOp",EDGE,"E7");Q14=makeQuery(id+"F3.opChamfer","BLEND_EDGE",EDGE,{"blendedFrom":[makeQuery(id+"F1.opExtrude","SWEPT_EDGE",EDGE,{"disambiguationData":[OSD([subQ1,subQ0])]}),makeQuery(id+"F1.opExtrude","CAP_FACE",FACE,{"disambiguationData":[OSD([sQuery(id+"F0.wireOp",EDGE,"E3.left"),sQuery(id+"F0.wireOp",EDGE,"E4"),sQuery(id+"F0.wireOp",EDGE,"E5"),sQuery(id+"F0.wireOp",EDGE,"E6"),subQ1,sQuery(id+"F0.wireOp",EDGE,"E12.0"),sQuery(id+"F0.wireOp",EDGE,"E12.1"),sQuery(id+"F0.wireOp",EDGE,"E12.2"),sQuery(id+"F0.wireOp",EDGE,"E12.3"),sQuery(id+"F0.wireOp",EDGE,"E12.4"),sQuery(id+"F0.wireOp",EDGE,"E12.5"),sQuery(id+"F0.wireOp",EDGE,"E13.MirrorCS"),sQuery(id+"F0.wireOp",EDGE,"E15.MirrorCS"),sQuery(id+"F0.wireOp",EDGE,"E18.MirrorCS"),sQuery(id+"F0.wireOp",EDGE,"E20.MirrorCS"),sQuery(id+"F0.wireOp",EDGE,"E14.MirrorCS"),sQuery(id+"F0.wireOp",EDGE,"E16.MirrorCS"),sQuery(id+"F0.wireOp",EDGE,"E19.MirrorCS"),sQuery(id+"F0.wireOp",EDGE,"E24.MirrorCS"),sQuery(id+"F0.wireOp",EDGE,"E25.MirrorCS"),sQuery(id+"F0.wireOp",EDGE,"E26.MirrorCS"),sQuery(id+"F0.wireOp",EDGE,"E27.MirrorCS"),sQuery(id+"F0.wireOp",EDGE,"E28.MirrorCS"),sQuery(id+"F0.wireOp",EDGE,"E29.MirrorCS"),sQuery(id+"F0.wireOp",EDGE,"E3.top"),subQ0,sQuery(id+"F0.wireOp",EDGE,"E37.MirrorCS"),sQuery(id+"F0.wireOp",EDGE,"E38.MirrorCS"),sQuery(id+"F0.wireOp",EDGE,"E35.MirrorCS"),sQuery(id+"F0.wireOp",EDGE,"E36.MirrorCS"),sQuery(id+"F0.wireOp",EDGE,"E33.MirrorCS"),sQuery(id+"F0.wireOp",EDGE,"E39.MirrorCS")])],"isStart":true})],"blendedInto":[makeQuery(id+"F1.opExtrude","CAP_FACE",FACE,{"disambiguationData":[OSD([sQuery(id+"F0.wireOp",EDGE,"E3.left"),sQuery(id+"F0.wireOp",EDGE,"E4"),sQuery(id+"F0.wireOp",EDGE,"E5"),sQuery(id+"F0.wireOp",EDGE,"E6"),subQ1,sQuery(id+"F0.wireOp",EDGE,"E12.0"),sQuery(id+"F0.wireOp",EDGE,"E12.1"),sQuery(id+"F0.wireOp",EDGE,"E12.2"),sQuery(id+"F0.wireOp",EDGE,"E12.3"),sQuery(id+"F0.wireOp",EDGE,"E12.4"),sQuery(id+"F0.wireOp",EDGE,"E12.5"),sQuery(id+"F0.wireOp",EDGE,"E13.MirrorCS"),sQuery(id+"F0.wireOp",EDGE,"E15.MirrorCS"),sQuery(id+"F0.wireOp",EDGE,"E18.MirrorCS"),sQuery(id+"F0.wireOp",EDGE,"E20.MirrorCS"),sQuery(id+"F0.wireOp",EDGE,"E14.MirrorCS"),sQuery(id+"F0.wireOp",EDGE,"E16.MirrorCS"),sQuery(id+"F0.wireOp",EDGE,"E19.MirrorCS"),sQuery(id+"F0.wireOp",EDGE,"E24.MirrorCS"),sQuery(id+"F0.wireOp",EDGE,"E25.MirrorCS"),sQuery(id+"F0.wireOp",EDGE,"E26.MirrorCS"),sQuery(id+"F0.wireOp",EDGE,"E27.MirrorCS"),sQuery(id+"F0.wireOp",EDGE,"E28.MirrorCS"),sQuery(id+"F0.wireOp",EDGE,"E29.MirrorCS"),sQuery(id+"F0.wireOp",EDGE,"E3.top"),subQ0,sQuery(id+"F0.wireOp",EDGE,"E37.MirrorCS"),sQuery(id+"F0.wireOp",EDGE,"E38.MirrorCS"),sQuery(id+"F0.wireOp",EDGE,"E35.MirrorCS"),sQuery(id+"F0.wireOp",EDGE,"E36.MirrorCS"),sQuery(id+"F0.wireOp",EDGE,"E33.MirrorCS"),sQuery(id+"F0.wireOp",EDGE,"E39.MirrorCS")])],"isStart":true})]});}
            var Q15;
            Q15=makeQuery(id+"F1.opExtrude","CAP_EDGE",EDGE,{"disambiguationData":[OSD([sQuery(id+"F0.wireOp",EDGE,"E4")])],"isStart":true});
            var Q16;
            Q16=makeQuery(id+"F1.opExtrude","CAP_EDGE",EDGE,{"disambiguationData":[OSD([sQuery(id+"F0.wireOp",EDGE,"E4")])],"isStart":false});
            var Q17;
            {var subQ0=sQuery(id+"F0.wireOp",EDGE,"E26.MirrorCS");var subQ1=sQuery(id+"F0.wireOp",EDGE,"E25.MirrorCS");var subQ2=sQuery(id+"F0.wireOp",EDGE,"E24.MirrorCS");var subQ3=sQuery(id+"F0.wireOp",EDGE,"E19.MirrorCS");var subQ4=sQuery(id+"F0.wireOp",EDGE,"E16.MirrorCS");var subQ5=sQuery(id+"F0.wireOp",EDGE,"E14.MirrorCS");var subQ6=sQuery(id+"F0.wireOp",EDGE,"E20.MirrorCS");var subQ7=sQuery(id+"F0.wireOp",EDGE,"E18.MirrorCS");var subQ8=sQuery(id+"F0.wireOp",EDGE,"E15.MirrorCS");var subQ9=sQuery(id+"F0.wireOp",EDGE,"E13.MirrorCS");var subQ10=sQuery(id+"F0.wireOp",EDGE,"E12.5");var subQ11=sQuery(id+"F0.wireOp",EDGE,"E5");var subQ12=sQuery(id+"F0.wireOp",EDGE,"E4");var subQ13=sQuery(id+"F0.wireOp",EDGE,"E6");var subQ14=sQuery(id+"F0.wireOp",EDGE,"E27.MirrorCS");var subQ15=sQuery(id+"F0.wireOp",EDGE,"E3.left");var subQ16=sQuery(id+"F0.wireOp",EDGE,"E12.4");var subQ17=sQuery(id+"F0.wireOp",EDGE,"E7");var subQ18=sQuery(id+"F0.wireOp",EDGE,"E12.0");var subQ19=sQuery(id+"F0.wireOp",EDGE,"E12.1");var subQ20=sQuery(id+"F0.wireOp",EDGE,"E12.2");var subQ21=sQuery(id+"F0.wireOp",EDGE,"E12.3");var subQ22=sQuery(id+"F0.wireOp",EDGE,"E28.MirrorCS");var subQ23=sQuery(id+"F0.wireOp",EDGE,"E29.MirrorCS");var subQ24=sQuery(id+"F0.wireOp",EDGE,"E3.top");var subQ25=sQuery(id+"F0.wireOp",EDGE,"E34.MirrorCS");var subQ26=sQuery(id+"F0.wireOp",EDGE,"E37.MirrorCS");var subQ27=sQuery(id+"F0.wireOp",EDGE,"E38.MirrorCS");var subQ28=sQuery(id+"F0.wireOp",EDGE,"E35.MirrorCS");var subQ29=sQuery(id+"F0.wireOp",EDGE,"E36.MirrorCS");var subQ30=sQuery(id+"F0.wireOp",EDGE,"E33.MirrorCS");var subQ31=sQuery(id+"F0.wireOp",EDGE,"E39.MirrorCS");Q17=makeQuery(id+"F3.opChamfer","BLEND_EDGE",EDGE,{"blendedFrom":[makeQuery(id+"F1.opExtrude","SWEPT_EDGE",EDGE,{"disambiguationData":[OSD([subQ12,subQ25])]}),makeQuery(id+"F2.boolean.opBoolean","SPLIT",FACE,{"disambiguationData":[TD([makeQuery(id+"F1.opExtrude","SWEPT_FACE",FACE,{"disambiguationData":[OSD([subQ15])]})])],"derivedFrom":makeQuery(id+"F1.opExtrude","CAP_FACE",FACE,{"disambiguationData":[OSD([subQ15,subQ12,subQ11,subQ13,subQ17,subQ18,subQ19,subQ20,subQ21,subQ16,subQ10,subQ9,subQ8,subQ7,subQ6,subQ5,subQ4,subQ3,subQ2,subQ1,subQ0,subQ14,subQ22,subQ23,subQ24,subQ25,subQ26,subQ27,subQ28,subQ29,subQ30,subQ31])],"isStart":false})})],"blendedInto":[makeQuery(id+"F2.boolean.opBoolean","SPLIT",FACE,{"disambiguationData":[TD([makeQuery(id+"F1.opExtrude","SWEPT_FACE",FACE,{"disambiguationData":[OSD([subQ15])]})])],"derivedFrom":makeQuery(id+"F1.opExtrude","CAP_FACE",FACE,{"disambiguationData":[OSD([subQ15,subQ12,subQ11,subQ13,subQ17,subQ18,subQ19,subQ20,subQ21,subQ16,subQ10,subQ9,subQ8,subQ7,subQ6,subQ5,subQ4,subQ3,subQ2,subQ1,subQ0,subQ14,subQ22,subQ23,subQ24,subQ25,subQ26,subQ27,subQ28,subQ29,subQ30,subQ31])],"isStart":false})})]});}
            var Q18;
            {var subQ0=sQuery(id+"F0.wireOp",EDGE,"E26.MirrorCS");var subQ1=sQuery(id+"F0.wireOp",EDGE,"E25.MirrorCS");var subQ2=sQuery(id+"F0.wireOp",EDGE,"E24.MirrorCS");var subQ3=sQuery(id+"F0.wireOp",EDGE,"E19.MirrorCS");var subQ4=sQuery(id+"F0.wireOp",EDGE,"E16.MirrorCS");var subQ5=sQuery(id+"F0.wireOp",EDGE,"E14.MirrorCS");var subQ6=sQuery(id+"F0.wireOp",EDGE,"E20.MirrorCS");var subQ7=sQuery(id+"F0.wireOp",EDGE,"E18.MirrorCS");var subQ8=sQuery(id+"F0.wireOp",EDGE,"E15.MirrorCS");var subQ9=sQuery(id+"F0.wireOp",EDGE,"E13.MirrorCS");var subQ10=sQuery(id+"F0.wireOp",EDGE,"E12.5");var subQ11=sQuery(id+"F0.wireOp",EDGE,"E5");var subQ12=sQuery(id+"F0.wireOp",EDGE,"E4");var subQ13=sQuery(id+"F0.wireOp",EDGE,"E6");var subQ14=sQuery(id+"F0.wireOp",EDGE,"E27.MirrorCS");var subQ15=sQuery(id+"F0.wireOp",EDGE,"E3.left");var subQ16=sQuery(id+"F0.wireOp",EDGE,"E12.4");var subQ17=sQuery(id+"F0.wireOp",EDGE,"E7");var subQ18=sQuery(id+"F0.wireOp",EDGE,"E12.0");var subQ19=sQuery(id+"F0.wireOp",EDGE,"E12.1");var subQ20=sQuery(id+"F0.wireOp",EDGE,"E12.2");var subQ21=sQuery(id+"F0.wireOp",EDGE,"E12.3");var subQ22=sQuery(id+"F0.wireOp",EDGE,"E28.MirrorCS");var subQ23=sQuery(id+"F0.wireOp",EDGE,"E29.MirrorCS");var subQ24=sQuery(id+"F0.wireOp",EDGE,"E3.top");var subQ25=sQuery(id+"F0.wireOp",EDGE,"E34.MirrorCS");var subQ26=sQuery(id+"F0.wireOp",EDGE,"E37.MirrorCS");var subQ27=sQuery(id+"F0.wireOp",EDGE,"E38.MirrorCS");var subQ28=sQuery(id+"F0.wireOp",EDGE,"E35.MirrorCS");var subQ29=sQuery(id+"F0.wireOp",EDGE,"E36.MirrorCS");var subQ30=sQuery(id+"F0.wireOp",EDGE,"E33.MirrorCS");var subQ31=sQuery(id+"F0.wireOp",EDGE,"E39.MirrorCS");Q18=makeQuery(id+"F3.opChamfer","BLEND_EDGE",EDGE,{"blendedFrom":[makeQuery(id+"F1.opExtrude","SWEPT_EDGE",EDGE,{"disambiguationData":[OSD([subQ12,subQ24])]}),makeQuery(id+"F2.boolean.opBoolean","SPLIT",FACE,{"disambiguationData":[TD([makeQuery(id+"F1.opExtrude","SWEPT_FACE",FACE,{"disambiguationData":[OSD([subQ15])]})])],"derivedFrom":makeQuery(id+"F1.opExtrude","CAP_FACE",FACE,{"disambiguationData":[OSD([subQ15,subQ12,subQ11,subQ13,subQ17,subQ18,subQ19,subQ20,subQ21,subQ16,subQ10,subQ9,subQ8,subQ7,subQ6,subQ5,subQ4,subQ3,subQ2,subQ1,subQ0,subQ14,subQ22,subQ23,subQ24,subQ25,subQ26,subQ27,subQ28,subQ29,subQ30,subQ31])],"isStart":false})})],"blendedInto":[makeQuery(id+"F2.boolean.opBoolean","SPLIT",FACE,{"disambiguationData":[TD([makeQuery(id+"F1.opExtrude","SWEPT_FACE",FACE,{"disambiguationData":[OSD([subQ15])]})])],"derivedFrom":makeQuery(id+"F1.opExtrude","CAP_FACE",FACE,{"disambiguationData":[OSD([subQ15,subQ12,subQ11,subQ13,subQ17,subQ18,subQ19,subQ20,subQ21,subQ16,subQ10,subQ9,subQ8,subQ7,subQ6,subQ5,subQ4,subQ3,subQ2,subQ1,subQ0,subQ14,subQ22,subQ23,subQ24,subQ25,subQ26,subQ27,subQ28,subQ29,subQ30,subQ31])],"isStart":false})})]});}
            var Q19;
            Q19=makeQuery(id+"F1.opExtrude","CAP_EDGE",EDGE,{"disambiguationData":[OSD([sQuery(id+"F0.wireOp",EDGE,"E3.top")])],"isStart":true});
            var Q20;
            Q20=makeQuery(id+"F1.opExtrude","CAP_EDGE",EDGE,{"disambiguationData":[OSD([sQuery(id+"F0.wireOp",EDGE,"E3.top")])],"isStart":false});
            var Q21;
            {var subQ0=sQuery(id+"F0.wireOp",EDGE,"E26.MirrorCS");var subQ1=sQuery(id+"F0.wireOp",EDGE,"E25.MirrorCS");var subQ2=sQuery(id+"F0.wireOp",EDGE,"E24.MirrorCS");var subQ3=sQuery(id+"F0.wireOp",EDGE,"E19.MirrorCS");var subQ4=sQuery(id+"F0.wireOp",EDGE,"E16.MirrorCS");var subQ5=sQuery(id+"F0.wireOp",EDGE,"E14.MirrorCS");var subQ6=sQuery(id+"F0.wireOp",EDGE,"E20.MirrorCS");var subQ7=sQuery(id+"F0.wireOp",EDGE,"E18.MirrorCS");var subQ8=sQuery(id+"F0.wireOp",EDGE,"E15.MirrorCS");var subQ9=sQuery(id+"F0.wireOp",EDGE,"E13.MirrorCS");var subQ10=sQuery(id+"F0.wireOp",EDGE,"E12.5");var subQ11=sQuery(id+"F0.wireOp",EDGE,"E5");var subQ12=sQuery(id+"F0.wireOp",EDGE,"E4");var subQ13=sQuery(id+"F0.wireOp",EDGE,"E6");var subQ14=sQuery(id+"F0.wireOp",EDGE,"E27.MirrorCS");var subQ15=sQuery(id+"F0.wireOp",EDGE,"E3.left");var subQ16=sQuery(id+"F0.wireOp",EDGE,"E12.4");var subQ17=sQuery(id+"F0.wireOp",EDGE,"E7");var subQ18=sQuery(id+"F0.wireOp",EDGE,"E12.0");var subQ19=sQuery(id+"F0.wireOp",EDGE,"E12.1");var subQ20=sQuery(id+"F0.wireOp",EDGE,"E12.2");var subQ21=sQuery(id+"F0.wireOp",EDGE,"E12.3");var subQ22=sQuery(id+"F0.wireOp",EDGE,"E28.MirrorCS");var subQ23=sQuery(id+"F0.wireOp",EDGE,"E29.MirrorCS");var subQ24=sQuery(id+"F0.wireOp",EDGE,"E3.top");var subQ25=sQuery(id+"F0.wireOp",EDGE,"E34.MirrorCS");var subQ26=sQuery(id+"F0.wireOp",EDGE,"E37.MirrorCS");var subQ27=sQuery(id+"F0.wireOp",EDGE,"E38.MirrorCS");var subQ28=sQuery(id+"F0.wireOp",EDGE,"E35.MirrorCS");var subQ29=sQuery(id+"F0.wireOp",EDGE,"E36.MirrorCS");var subQ30=sQuery(id+"F0.wireOp",EDGE,"E33.MirrorCS");var subQ31=sQuery(id+"F0.wireOp",EDGE,"E39.MirrorCS");Q21=makeQuery(id+"F3.opChamfer","BLEND_EDGE",EDGE,{"blendedFrom":[makeQuery(id+"F1.opExtrude","SWEPT_EDGE",EDGE,{"disambiguationData":[OSD([subQ11,subQ24])]}),makeQuery(id+"F2.boolean.opBoolean","SPLIT",FACE,{"disambiguationData":[TD([makeQuery(id+"F1.opExtrude","SWEPT_FACE",FACE,{"disambiguationData":[OSD([subQ15])]})])],"derivedFrom":makeQuery(id+"F1.opExtrude","CAP_FACE",FACE,{"disambiguationData":[OSD([subQ15,subQ12,subQ11,subQ13,subQ17,subQ18,subQ19,subQ20,subQ21,subQ16,subQ10,subQ9,subQ8,subQ7,subQ6,subQ5,subQ4,subQ3,subQ2,subQ1,subQ0,subQ14,subQ22,subQ23,subQ24,subQ25,subQ26,subQ27,subQ28,subQ29,subQ30,subQ31])],"isStart":false})})],"blendedInto":[makeQuery(id+"F2.boolean.opBoolean","SPLIT",FACE,{"disambiguationData":[TD([makeQuery(id+"F1.opExtrude","SWEPT_FACE",FACE,{"disambiguationData":[OSD([subQ15])]})])],"derivedFrom":makeQuery(id+"F1.opExtrude","CAP_FACE",FACE,{"disambiguationData":[OSD([subQ15,subQ12,subQ11,subQ13,subQ17,subQ18,subQ19,subQ20,subQ21,subQ16,subQ10,subQ9,subQ8,subQ7,subQ6,subQ5,subQ4,subQ3,subQ2,subQ1,subQ0,subQ14,subQ22,subQ23,subQ24,subQ25,subQ26,subQ27,subQ28,subQ29,subQ30,subQ31])],"isStart":false})})]});}
            var Q22;
            {var subQ0=sQuery(id+"F0.wireOp",EDGE,"E3.top");var subQ1=sQuery(id+"F0.wireOp",EDGE,"E5");Q22=makeQuery(id+"F3.opChamfer","BLEND_EDGE",EDGE,{"blendedFrom":[makeQuery(id+"F1.opExtrude","SWEPT_EDGE",EDGE,{"disambiguationData":[OSD([subQ1,subQ0])]}),makeQuery(id+"F1.opExtrude","CAP_FACE",FACE,{"disambiguationData":[OSD([sQuery(id+"F0.wireOp",EDGE,"E3.left"),sQuery(id+"F0.wireOp",EDGE,"E4"),subQ1,sQuery(id+"F0.wireOp",EDGE,"E6"),sQuery(id+"F0.wireOp",EDGE,"E7"),sQuery(id+"F0.wireOp",EDGE,"E12.0"),sQuery(id+"F0.wireOp",EDGE,"E12.1"),sQuery(id+"F0.wireOp",EDGE,"E12.2"),sQuery(id+"F0.wireOp",EDGE,"E12.3"),sQuery(id+"F0.wireOp",EDGE,"E12.4"),sQuery(id+"F0.wireOp",EDGE,"E12.5"),sQuery(id+"F0.wireOp",EDGE,"E13.MirrorCS"),sQuery(id+"F0.wireOp",EDGE,"E15.MirrorCS"),sQuery(id+"F0.wireOp",EDGE,"E18.MirrorCS"),sQuery(id+"F0.wireOp",EDGE,"E20.MirrorCS"),sQuery(id+"F0.wireOp",EDGE,"E14.MirrorCS"),sQuery(id+"F0.wireOp",EDGE,"E16.MirrorCS"),sQuery(id+"F0.wireOp",EDGE,"E19.MirrorCS"),sQuery(id+"F0.wireOp",EDGE,"E24.MirrorCS"),sQuery(id+"F0.wireOp",EDGE,"E25.MirrorCS"),sQuery(id+"F0.wireOp",EDGE,"E26.MirrorCS"),sQuery(id+"F0.wireOp",EDGE,"E27.MirrorCS"),sQuery(id+"F0.wireOp",EDGE,"E28.MirrorCS"),sQuery(id+"F0.wireOp",EDGE,"E29.MirrorCS"),subQ0,sQuery(id+"F0.wireOp",EDGE,"E34.MirrorCS"),sQuery(id+"F0.wireOp",EDGE,"E37.MirrorCS"),sQuery(id+"F0.wireOp",EDGE,"E38.MirrorCS"),sQuery(id+"F0.wireOp",EDGE,"E35.MirrorCS"),sQuery(id+"F0.wireOp",EDGE,"E36.MirrorCS"),sQuery(id+"F0.wireOp",EDGE,"E33.MirrorCS"),sQuery(id+"F0.wireOp",EDGE,"E39.MirrorCS")])],"isStart":true})],"blendedInto":[makeQuery(id+"F1.opExtrude","CAP_FACE",FACE,{"disambiguationData":[OSD([sQuery(id+"F0.wireOp",EDGE,"E3.left"),sQuery(id+"F0.wireOp",EDGE,"E4"),subQ1,sQuery(id+"F0.wireOp",EDGE,"E6"),sQuery(id+"F0.wireOp",EDGE,"E7"),sQuery(id+"F0.wireOp",EDGE,"E12.0"),sQuery(id+"F0.wireOp",EDGE,"E12.1"),sQuery(id+"F0.wireOp",EDGE,"E12.2"),sQuery(id+"F0.wireOp",EDGE,"E12.3"),sQuery(id+"F0.wireOp",EDGE,"E12.4"),sQuery(id+"F0.wireOp",EDGE,"E12.5"),sQuery(id+"F0.wireOp",EDGE,"E13.MirrorCS"),sQuery(id+"F0.wireOp",EDGE,"E15.MirrorCS"),sQuery(id+"F0.wireOp",EDGE,"E18.MirrorCS"),sQuery(id+"F0.wireOp",EDGE,"E20.MirrorCS"),sQuery(id+"F0.wireOp",EDGE,"E14.MirrorCS"),sQuery(id+"F0.wireOp",EDGE,"E16.MirrorCS"),sQuery(id+"F0.wireOp",EDGE,"E19.MirrorCS"),sQuery(id+"F0.wireOp",EDGE,"E24.MirrorCS"),sQuery(id+"F0.wireOp",EDGE,"E25.MirrorCS"),sQuery(id+"F0.wireOp",EDGE,"E26.MirrorCS"),sQuery(id+"F0.wireOp",EDGE,"E27.MirrorCS"),sQuery(id+"F0.wireOp",EDGE,"E28.MirrorCS"),sQuery(id+"F0.wireOp",EDGE,"E29.MirrorCS"),subQ0,sQuery(id+"F0.wireOp",EDGE,"E34.MirrorCS"),sQuery(id+"F0.wireOp",EDGE,"E37.MirrorCS"),sQuery(id+"F0.wireOp",EDGE,"E38.MirrorCS"),sQuery(id+"F0.wireOp",EDGE,"E35.MirrorCS"),sQuery(id+"F0.wireOp",EDGE,"E36.MirrorCS"),sQuery(id+"F0.wireOp",EDGE,"E33.MirrorCS"),sQuery(id+"F0.wireOp",EDGE,"E39.MirrorCS")])],"isStart":true})]});}
            fillet(context, id + "F4", {"entities" : qUnion([Q0, Q1, Q2, Q3, Q4, Q5, Q6, Q7, Q8, Q9, Q10, Q11, Q12, Q13, Q14, Q15, Q16, Q17, Q18, Q19, Q20, Q21, Q22]), "radius" : 1 * mm, "tangentPropagation" : true, "allowEdgeOverflow" : false});
        }
        {
            var Q0;
            {var subQ4=sQuery(id+"F0.wireOp",EDGE,"E15.MirrorCS");Q0=makeQuery(id+"F0.imprint","IMPRINT",FACE,{"disambiguationData":[TD([[makeQuery(id+"F0.imprint","IMPRINT",EDGE,{"derivedFrom":subQ4}),1.0]])]});}
            var Q1;
            Q1=makeQuery(id+"F0.imprint","IMPRINT",FACE,{"disambiguationData":[TD([[makeQuery(id+"F0.imprint","IMPRINT",EDGE,{"derivedFrom":sQuery(id+"F0.wireOp",EDGE,"E12.0")}),-1.0]])]});
            var Q2;
            {var subQ5=sQuery(id+"F0.wireOp",EDGE,"E20.MirrorCS");Q2=makeQuery(id+"F0.imprint","IMPRINT",FACE,{"disambiguationData":[TD([[makeQuery(id+"F0.imprint","IMPRINT",EDGE,{"derivedFrom":subQ5}),1.0]])]});}
            var Q3;
            {var subQ0=sQuery(id+"F0.wireOp",EDGE,"E12.4");Q3=makeQuery(id+"F0.imprint","IMPRINT",FACE,{"disambiguationData":[TD([[makeQuery(id+"F0.imprint","IMPRINT",EDGE,{"derivedFrom":subQ0}),-1.0]])]});}
            var Q4;
            {var subQ0=sQuery(id+"F0.wireOp",EDGE,"E38.MirrorCS");Q4=makeQuery(id+"F0.imprint","IMPRINT",FACE,{"disambiguationData":[TD([[makeQuery(id+"F0.imprint","IMPRINT",EDGE,{"derivedFrom":subQ0}),-1.0]])]});}
            var Q5;
            {var subQ0=sQuery(id+"F0.wireOp",EDGE,"E37.MirrorCS");Q5=makeQuery(id+"F0.imprint","IMPRINT",FACE,{"disambiguationData":[TD([[makeQuery(id+"F0.imprint","IMPRINT",EDGE,{"derivedFrom":subQ0}),-1.0]])]});}
            var Q6;
            {var subQ0=sQuery(id+"F0.wireOp",EDGE,"E28.MirrorCS");Q6=makeQuery(id+"F0.imprint","IMPRINT",FACE,{"disambiguationData":[TD([[makeQuery(id+"F0.imprint","IMPRINT",EDGE,{"derivedFrom":subQ0}),1.0]])]});}
            var Q7;
            {var subQ0=sQuery(id+"F0.wireOp",EDGE,"E24.MirrorCS");Q7=makeQuery(id+"F0.imprint","IMPRINT",FACE,{"disambiguationData":[TD([[makeQuery(id+"F0.imprint","IMPRINT",EDGE,{"derivedFrom":subQ0}),1.0]])]});}
            var Q8;
            {var subQ0=sQuery(id+"F0.wireOp",EDGE,"E26.MirrorCS");var subQ1=sQuery(id+"F0.wireOp",EDGE,"E25.MirrorCS");var subQ2=sQuery(id+"F0.wireOp",EDGE,"E24.MirrorCS");var subQ3=sQuery(id+"F0.wireOp",EDGE,"E19.MirrorCS");var subQ4=sQuery(id+"F0.wireOp",EDGE,"E16.MirrorCS");var subQ5=sQuery(id+"F0.wireOp",EDGE,"E14.MirrorCS");var subQ6=sQuery(id+"F0.wireOp",EDGE,"E20.MirrorCS");var subQ7=sQuery(id+"F0.wireOp",EDGE,"E18.MirrorCS");var subQ8=sQuery(id+"F0.wireOp",EDGE,"E15.MirrorCS");var subQ9=sQuery(id+"F0.wireOp",EDGE,"E13.MirrorCS");var subQ10=sQuery(id+"F0.wireOp",EDGE,"E12.5");var subQ11=sQuery(id+"F0.wireOp",EDGE,"E5");var subQ12=sQuery(id+"F0.wireOp",EDGE,"E4");var subQ13=sQuery(id+"F0.wireOp",EDGE,"E6");var subQ14=sQuery(id+"F0.wireOp",EDGE,"E27.MirrorCS");var subQ15=sQuery(id+"F0.wireOp",EDGE,"E3.left");var subQ16=sQuery(id+"F0.wireOp",EDGE,"E12.4");var subQ17=sQuery(id+"F0.wireOp",EDGE,"E7");var subQ18=sQuery(id+"F0.wireOp",EDGE,"E12.0");var subQ19=sQuery(id+"F0.wireOp",EDGE,"E12.1");var subQ20=sQuery(id+"F0.wireOp",EDGE,"E12.2");var subQ21=sQuery(id+"F0.wireOp",EDGE,"E12.3");var subQ22=sQuery(id+"F0.wireOp",EDGE,"E28.MirrorCS");var subQ23=sQuery(id+"F0.wireOp",EDGE,"E29.MirrorCS");var subQ24=sQuery(id+"F0.wireOp",EDGE,"E3.top");var subQ25=sQuery(id+"F0.wireOp",EDGE,"E34.MirrorCS");var subQ26=sQuery(id+"F0.wireOp",EDGE,"E37.MirrorCS");var subQ27=sQuery(id+"F0.wireOp",EDGE,"E38.MirrorCS");var subQ28=sQuery(id+"F0.wireOp",EDGE,"E35.MirrorCS");var subQ29=sQuery(id+"F0.wireOp",EDGE,"E36.MirrorCS");var subQ30=sQuery(id+"F0.wireOp",EDGE,"E33.MirrorCS");var subQ31=sQuery(id+"F0.wireOp",EDGE,"E39.MirrorCS");Q8=makeQuery(id+"F2.boolean.opBoolean","SPLIT",FACE,{"disambiguationData":[TD([makeQuery(id+"F1.opExtrude","SWEPT_FACE",FACE,{"disambiguationData":[OSD([subQ15])]})])],"derivedFrom":makeQuery(id+"F1.opExtrude","CAP_FACE",FACE,{"disambiguationData":[OSD([subQ15,subQ12,subQ11,subQ13,subQ17,subQ18,subQ19,subQ20,subQ21,subQ16,subQ10,subQ9,subQ8,subQ7,subQ6,subQ5,subQ4,subQ3,subQ2,subQ1,subQ0,subQ14,subQ22,subQ23,subQ24,subQ25,subQ26,subQ27,subQ28,subQ29,subQ30,subQ31])],"isStart":false})});}
            var Q9;
            {var subQ0=sQuery(id+"F0.wireOp",EDGE,"E26.MirrorCS");var subQ1=sQuery(id+"F0.wireOp",EDGE,"E25.MirrorCS");var subQ2=sQuery(id+"F0.wireOp",EDGE,"E24.MirrorCS");var subQ3=sQuery(id+"F0.wireOp",EDGE,"E19.MirrorCS");var subQ4=sQuery(id+"F0.wireOp",EDGE,"E16.MirrorCS");var subQ5=sQuery(id+"F0.wireOp",EDGE,"E14.MirrorCS");var subQ6=sQuery(id+"F0.wireOp",EDGE,"E20.MirrorCS");var subQ7=sQuery(id+"F0.wireOp",EDGE,"E18.MirrorCS");var subQ8=sQuery(id+"F0.wireOp",EDGE,"E15.MirrorCS");var subQ9=sQuery(id+"F0.wireOp",EDGE,"E13.MirrorCS");var subQ10=sQuery(id+"F0.wireOp",EDGE,"E12.5");var subQ11=sQuery(id+"F0.wireOp",EDGE,"E5");var subQ12=sQuery(id+"F0.wireOp",EDGE,"E4");var subQ13=sQuery(id+"F0.wireOp",EDGE,"E6");var subQ14=sQuery(id+"F0.wireOp",EDGE,"E27.MirrorCS");var subQ15=sQuery(id+"F0.wireOp",EDGE,"E3.left");var subQ16=sQuery(id+"F0.wireOp",EDGE,"E12.4");var subQ17=sQuery(id+"F0.wireOp",EDGE,"E7");var subQ18=sQuery(id+"F0.wireOp",EDGE,"E12.0");var subQ19=sQuery(id+"F0.wireOp",EDGE,"E12.1");var subQ20=sQuery(id+"F0.wireOp",EDGE,"E12.2");var subQ21=sQuery(id+"F0.wireOp",EDGE,"E12.3");var subQ22=sQuery(id+"F0.wireOp",EDGE,"E28.MirrorCS");var subQ23=sQuery(id+"F0.wireOp",EDGE,"E29.MirrorCS");var subQ24=sQuery(id+"F0.wireOp",EDGE,"E3.top");var subQ25=sQuery(id+"F0.wireOp",EDGE,"E34.MirrorCS");var subQ26=sQuery(id+"F0.wireOp",EDGE,"E37.MirrorCS");var subQ27=sQuery(id+"F0.wireOp",EDGE,"E38.MirrorCS");var subQ28=sQuery(id+"F0.wireOp",EDGE,"E35.MirrorCS");var subQ29=sQuery(id+"F0.wireOp",EDGE,"E36.MirrorCS");var subQ30=sQuery(id+"F0.wireOp",EDGE,"E33.MirrorCS");var subQ31=sQuery(id+"F0.wireOp",EDGE,"E39.MirrorCS");Q9=makeQuery(id+"F2.boolean.opBoolean","SPLIT",FACE,{"disambiguationData":[TD([makeQuery(id+"F1.opExtrude","SWEPT_FACE",FACE,{"disambiguationData":[OSD([subQ15])]})])],"derivedFrom":makeQuery(id+"F1.opExtrude","CAP_FACE",FACE,{"disambiguationData":[OSD([subQ15,subQ12,subQ11,subQ13,subQ17,subQ18,subQ19,subQ20,subQ21,subQ16,subQ10,subQ9,subQ8,subQ7,subQ6,subQ5,subQ4,subQ3,subQ2,subQ1,subQ0,subQ14,subQ22,subQ23,subQ24,subQ25,subQ26,subQ27,subQ28,subQ29,subQ30,subQ31])],"isStart":false})});}
            extrude(context, id + "F5", {"entities" : qUnion([Q0, Q1, Q2, Q3, Q4, Q5, Q6, Q7]), "operationType" : NewBodyOperationType.ADD, "endBound" : BoundingType.UP_TO_SURFACE, "depth" : 4 * mm, "endBoundEntityFace" : qUnion([Q8]), "offsetDistance" : 25 * mm, "hasSecondDirection" : true, "secondDirectionBound" : SecondDirectionBoundingType.UP_TO_SURFACE, "secondDirectionOppositeDirection" : false, "secondDirectionDepth" : 2 * mm, "secondDirectionBoundEntityFace" : qUnion([Q9]), "hasSecondDirectionOffset" : true, "secondDirectionOffsetDistance" : 1 * mm});
        }
        {
            var Q0;
            Q0=makeQuery(id+"F1.opExtrude","SWEPT_EDGE",EDGE,{"disambiguationData":[OSD([sQuery(id+"F0.wireOp",EDGE,"E1.top"),sQuery(id+"F0.wireOp",EDGE,"E43")])]});
            var Q1;
            Q1=makeQuery(id+"F1.opExtrude","SWEPT_EDGE",EDGE,{"disambiguationData":[OSD([sQuery(id+"F0.wireOp",EDGE,"E1.left"),sQuery(id+"F0.wireOp",EDGE,"E42")])]});
            var Q2;
            Q2=makeQuery(id+"F1.opExtrude","SWEPT_EDGE",EDGE,{"disambiguationData":[OSD([sQuery(id+"F0.wireOp",EDGE,"E1.top"),sQuery(id+"F0.wireOp",EDGE,"E41")])]});
            var Q3;
            Q3=makeQuery(id+"F1.opExtrude","SWEPT_EDGE",EDGE,{"disambiguationData":[OSD([sQuery(id+"F0.wireOp",EDGE,"E1.right"),sQuery(id+"F0.wireOp",EDGE,"E40")])]});
            var Q4;
            Q4=makeQuery(id+"F1.opExtrude","SWEPT_EDGE",EDGE,{"disambiguationData":[OSD([sQuery(id+"F0.wireOp",EDGE,"E40"),sQuery(id+"F0.wireOp",EDGE,"E43")])]});
            var Q5;
            Q5=makeQuery(id+"F1.opExtrude","SWEPT_EDGE",EDGE,{"disambiguationData":[OSD([sQuery(id+"F0.wireOp",EDGE,"E41"),sQuery(id+"F0.wireOp",EDGE,"E43")])]});
            var Q6;
            Q6=makeQuery(id+"F1.opExtrude","SWEPT_EDGE",EDGE,{"disambiguationData":[OSD([sQuery(id+"F0.wireOp",EDGE,"E41"),sQuery(id+"F0.wireOp",EDGE,"E42")])]});
            var Q7;
            Q7=makeQuery(id+"F1.opExtrude","SWEPT_EDGE",EDGE,{"disambiguationData":[OSD([sQuery(id+"F0.wireOp",EDGE,"E40"),sQuery(id+"F0.wireOp",EDGE,"E42")])]});
            var Q8;
            Q8=makeQuery(id+"F1.opExtrude","SWEPT_EDGE",EDGE,{"disambiguationData":[OSD([sQuery(id+"F0.wireOp",EDGE,"E1.left"),sQuery(id+"F0.wireOp",EDGE,"E41")])]});
            var Q9;
            Q9=makeQuery(id+"F1.opExtrude","SWEPT_EDGE",EDGE,{"disambiguationData":[OSD([sQuery(id+"F0.wireOp",EDGE,"E1.bottom"),sQuery(id+"F0.wireOp",EDGE,"E40")])]});
            var Q10;
            Q10=makeQuery(id+"F1.opExtrude","SWEPT_EDGE",EDGE,{"disambiguationData":[OSD([sQuery(id+"F0.wireOp",EDGE,"E1.bottom"),sQuery(id+"F0.wireOp",EDGE,"E42")])]});
            var Q11;
            Q11=makeQuery(id+"F1.opExtrude","SWEPT_EDGE",EDGE,{"disambiguationData":[OSD([sQuery(id+"F0.wireOp",EDGE,"E1.right"),sQuery(id+"F0.wireOp",EDGE,"E43")])]});
            chamfer(context, id + "F6", {"entities" : qUnion([Q0, Q1, Q2, Q3, Q4, Q5, Q6, Q7, Q8, Q9, Q10, Q11]), "width" : 1 * mm, "tangentPropagation" : true});
        }
        {
            var Q0;
            {var subQ0=sQuery(id+"F0.wireOp",EDGE,"E40");Q0=makeQuery(id+"F1.opExtrude","CAP_EDGE",EDGE,{"disambiguationData":[OSD([subQ0]),TDD([makeQuery(id+"F0.imprint","IMPRINT",EDGE,{"disambiguationData":[TD([[makeQuery(id+"F0.imprint","INTERSECT",VERTEX,{"derivedFrom":[sQuery(id+"F0.wireOp",EDGE,"E1.right"),subQ0]}),-1.0]])],"derivedFrom":subQ0})])],"isStart":false});}
            var Q1;
            {var subQ0=sQuery(id+"F0.wireOp",EDGE,"E43");Q1=makeQuery(id+"F1.opExtrude","CAP_EDGE",EDGE,{"disambiguationData":[OSD([subQ0]),TDD([makeQuery(id+"F0.imprint","IMPRINT",EDGE,{"disambiguationData":[TD([[makeQuery(id+"F0.imprint","INTERSECT",VERTEX,{"derivedFrom":[sQuery(id+"F0.wireOp",EDGE,"E1.right"),subQ0]}),1.0]])],"derivedFrom":subQ0})])],"isStart":false});}
            var Q2;
            {var subQ0=sQuery(id+"F0.wireOp",EDGE,"E42");Q2=makeQuery(id+"F1.opExtrude","CAP_EDGE",EDGE,{"disambiguationData":[OSD([subQ0]),TDD([makeQuery(id+"F0.imprint","IMPRINT",EDGE,{"disambiguationData":[TD([[makeQuery(id+"F0.imprint","INTERSECT",VERTEX,{"derivedFrom":[sQuery(id+"F0.wireOp",EDGE,"E1.bottom"),subQ0]}),1.0]])],"derivedFrom":subQ0})])],"isStart":false});}
            var Q3;
            {var subQ0=sQuery(id+"F0.wireOp",EDGE,"E40");Q3=makeQuery(id+"F1.opExtrude","CAP_EDGE",EDGE,{"disambiguationData":[OSD([subQ0]),TDD([makeQuery(id+"F0.imprint","IMPRINT",EDGE,{"disambiguationData":[TD([[makeQuery(id+"F0.imprint","INTERSECT",VERTEX,{"derivedFrom":[sQuery(id+"F0.wireOp",EDGE,"E1.bottom"),subQ0]}),1.0]])],"derivedFrom":subQ0})])],"isStart":false});}
            var Q4;
            {var subQ0=sQuery(id+"F0.wireOp",EDGE,"E40");Q4=makeQuery(id+"F1.opExtrude","CAP_EDGE",EDGE,{"disambiguationData":[OSD([subQ0]),TDD([makeQuery(id+"F0.imprint","IMPRINT",EDGE,{"disambiguationData":[TD([[makeQuery(id+"F0.imprint","INTERSECT",VERTEX,{"derivedFrom":[sQuery(id+"F0.wireOp",EDGE,"E1.bottom"),subQ0]}),1.0]])],"derivedFrom":subQ0})])],"isStart":true});}
            var Q5;
            {var subQ0=sQuery(id+"F0.wireOp",EDGE,"E41");Q5=makeQuery(id+"F1.opExtrude","CAP_EDGE",EDGE,{"disambiguationData":[OSD([subQ0]),TDD([makeQuery(id+"F0.imprint","IMPRINT",EDGE,{"disambiguationData":[TD([[makeQuery(id+"F0.imprint","INTERSECT",VERTEX,{"derivedFrom":[sQuery(id+"F0.wireOp",EDGE,"E1.left"),subQ0]}),1.0]])],"derivedFrom":subQ0})])],"isStart":false});}
            var Q6;
            {var subQ0=sQuery(id+"F0.wireOp",EDGE,"E42");Q6=makeQuery(id+"F1.opExtrude","CAP_EDGE",EDGE,{"disambiguationData":[OSD([subQ0]),TDD([makeQuery(id+"F0.imprint","IMPRINT",EDGE,{"disambiguationData":[TD([[makeQuery(id+"F0.imprint","INTERSECT",VERTEX,{"derivedFrom":[sQuery(id+"F0.wireOp",EDGE,"E1.left"),subQ0]}),-1.0]])],"derivedFrom":subQ0})])],"isStart":false});}
            var Q7;
            {var subQ0=sQuery(id+"F0.wireOp",EDGE,"E43");Q7=makeQuery(id+"F1.opExtrude","CAP_EDGE",EDGE,{"disambiguationData":[OSD([subQ0]),TDD([makeQuery(id+"F0.imprint","IMPRINT",EDGE,{"disambiguationData":[TD([[makeQuery(id+"F0.imprint","INTERSECT",VERTEX,{"derivedFrom":[sQuery(id+"F0.wireOp",EDGE,"E1.top"),subQ0]}),-1.0]])],"derivedFrom":subQ0})])],"isStart":false});}
            var Q8;
            {var subQ0=sQuery(id+"F0.wireOp",EDGE,"E41");Q8=makeQuery(id+"F1.opExtrude","CAP_EDGE",EDGE,{"disambiguationData":[OSD([subQ0]),TDD([makeQuery(id+"F0.imprint","IMPRINT",EDGE,{"disambiguationData":[TD([[makeQuery(id+"F0.imprint","INTERSECT",VERTEX,{"derivedFrom":[sQuery(id+"F0.wireOp",EDGE,"E1.top"),subQ0]}),-1.0]])],"derivedFrom":subQ0})])],"isStart":false});}
            var Q9;
            {var subQ0=sQuery(id+"F0.wireOp",EDGE,"E43");Q9=makeQuery(id+"F1.opExtrude","CAP_EDGE",EDGE,{"disambiguationData":[OSD([subQ0]),TDD([makeQuery(id+"F0.imprint","IMPRINT",EDGE,{"disambiguationData":[TD([[makeQuery(id+"F0.imprint","INTERSECT",VERTEX,{"derivedFrom":[sQuery(id+"F0.wireOp",EDGE,"E1.right"),subQ0]}),1.0]])],"derivedFrom":subQ0})])],"isStart":true});}
            var Q10;
            {var subQ0=sQuery(id+"F0.wireOp",EDGE,"E42");Q10=makeQuery(id+"F1.opExtrude","CAP_EDGE",EDGE,{"disambiguationData":[OSD([subQ0]),TDD([makeQuery(id+"F0.imprint","IMPRINT",EDGE,{"disambiguationData":[TD([[makeQuery(id+"F0.imprint","INTERSECT",VERTEX,{"derivedFrom":[sQuery(id+"F0.wireOp",EDGE,"E1.bottom"),subQ0]}),1.0]])],"derivedFrom":subQ0})])],"isStart":true});}
            var Q11;
            {var subQ0=sQuery(id+"F0.wireOp",EDGE,"E43");Q11=makeQuery(id+"F1.opExtrude","CAP_EDGE",EDGE,{"disambiguationData":[OSD([subQ0]),TDD([makeQuery(id+"F0.imprint","IMPRINT",EDGE,{"disambiguationData":[TD([[makeQuery(id+"F0.imprint","INTERSECT",VERTEX,{"derivedFrom":[sQuery(id+"F0.wireOp",EDGE,"E1.top"),subQ0]}),-1.0]])],"derivedFrom":subQ0})])],"isStart":true});}
            var Q12;
            {var subQ0=sQuery(id+"F0.wireOp",EDGE,"E42");Q12=makeQuery(id+"F1.opExtrude","CAP_EDGE",EDGE,{"disambiguationData":[OSD([subQ0]),TDD([makeQuery(id+"F0.imprint","IMPRINT",EDGE,{"disambiguationData":[TD([[makeQuery(id+"F0.imprint","INTERSECT",VERTEX,{"derivedFrom":[sQuery(id+"F0.wireOp",EDGE,"E1.left"),subQ0]}),-1.0]])],"derivedFrom":subQ0})])],"isStart":true});}
            var Q13;
            {var subQ0=sQuery(id+"F0.wireOp",EDGE,"E40");Q13=makeQuery(id+"F1.opExtrude","CAP_EDGE",EDGE,{"disambiguationData":[OSD([subQ0]),TDD([makeQuery(id+"F0.imprint","IMPRINT",EDGE,{"disambiguationData":[TD([[makeQuery(id+"F0.imprint","INTERSECT",VERTEX,{"derivedFrom":[sQuery(id+"F0.wireOp",EDGE,"E1.right"),subQ0]}),-1.0]])],"derivedFrom":subQ0})])],"isStart":true});}
            fillet(context, id + "F7", {"entities" : qUnion([Q0, Q1, Q2, Q3, Q4, Q5, Q6, Q7, Q8, Q9, Q10, Q11, Q12, Q13]), "radius" : 1 * mm, "tangentPropagation" : true, "allowEdgeOverflow" : false});
        }
    });
